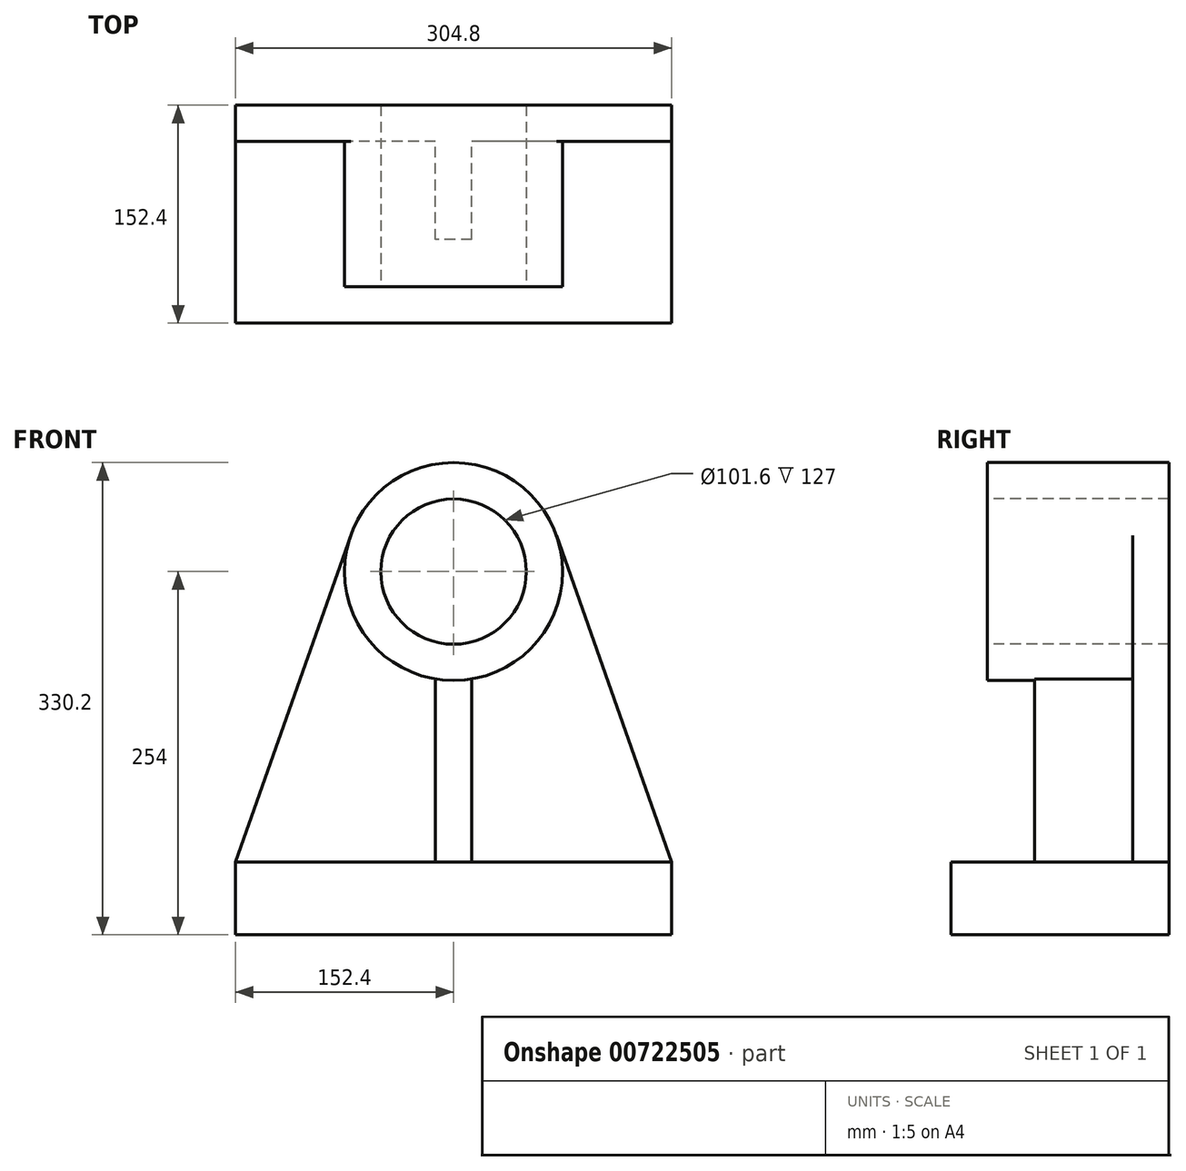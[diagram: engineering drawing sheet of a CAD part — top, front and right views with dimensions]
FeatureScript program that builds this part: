
annotation { "Feature Type Name" : "Feature", "Feature Type Description" : "" }
export const myFeature = defineFeature(function(context is Context, id is Id, definition is map)
    precondition{}
    {
        {
            var Q0;
            Q0=qCreatedBy(makeId("Top.planeOp"),FACE);
            var sketch = newSketch(context, id + "F0", { "sketchPlane" : qUnion([Q0])});
            skLineSegment(sketch, "E0.bottom", {"start": v(152.4, -76.2) * mm, "end": v(-152.4, -76.2) * mm});
            skLineSegment(sketch, "E0.top", {"start": v(152.4, 76.2) * mm, "end": v(-152.4, 76.2) * mm});
            skLineSegment(sketch, "E0.left", {"start": v(152.4, -76.2) * mm, "end": v(152.4, 76.2) * mm});
            skLineSegment(sketch, "E0.right", {"start": v(-152.4, -76.2) * mm, "end": v(-152.4, 76.2) * mm});
            skPoint(sketch, "E0.middle", {"position": v(0, 0) * mm});
            skSolve(sketch);
        }
        {
            var Q0;
            Q0 = qSketchRegion(id + "F0", true);
            extrude(context, id + "F1", {"entities" : qUnion([Q0]), "depth" : 50.8 * mm, "offsetDistance" : 25.4 * mm});
        }
        {
            var Q0;
            Q0=makeQuery(id+"F1.opExtrude","SWEPT_FACE",FACE,{"disambiguationData":[OSD([sQuery(id+"F0.wireOp",EDGE,"E0.top")])]});
            var sketch = newSketch(context, id + "F2", { "sketchPlane" : qUnion([Q0])});
            skLineSegment(sketch, "E1", {"start": v(0, 0) * mm, "end": v(0, 254) * mm, "construction": true});
            skLineSegment(sketch, "E2", {"start": v(-152.4, 50.8) * mm, "end": v(152.4, 50.8) * mm});
            skArc(sketch, "E3", {"start": v(71.87, 279.33) * mm, "mid": v(0, 330.2) * mm, "end": v(-71.87, 279.33) * mm});
            skLineSegment(sketch, "E4", {"start": v(-152.4, 50.8) * mm, "end": v(-71.87, 279.33) * mm});
            skLineSegment(sketch, "E5", {"start": v(152.4, 50.8) * mm, "end": v(71.87, 279.33) * mm});
            skSolve(sketch);
        }
        {
            var Q0;
            Q0 = qSketchRegion(id + "F2", true);
            extrude(context, id + "F3", {"entities" : qUnion([Q0]), "operationType" : NewBodyOperationType.ADD, "oppositeDirection" : true, "depth" : 25.4 * mm, "offsetDistance" : 25.4 * mm});
        }
        {
            var Q0;
            Q0=makeQuery(id+"F3.opExtrude","CAP_FACE",FACE,{"disambiguationData":[OSD([sQuery(id+"F2.wireOp",EDGE,"E2"),sQuery(id+"F2.wireOp",EDGE,"E3"),sQuery(id+"F2.wireOp",EDGE,"E4"),sQuery(id+"F2.wireOp",EDGE,"E5")])],"isStart":false});
            var sketch = newSketch(context, id + "F4", { "sketchPlane" : qUnion([Q0])});
            skCircle(sketch, "E6", {"center": v(0, 254) * mm, "radius": 76.2 * mm});
            skSolve(sketch);
        }
        {
            var Q0;
            Q0 = qSketchRegion(id + "F4", true);
            extrude(context, id + "F5", {"entities" : qUnion([Q0]), "operationType" : NewBodyOperationType.ADD, "depth" : 101.6 * mm, "offsetDistance" : 25.4 * mm});
        }
        {
            var Q0;
            Q0=makeQuery(id+"F5.opExtrude","CAP_FACE",FACE,{"disambiguationData":[OSD([sQuery(id+"F4.wireOp",EDGE,"E6")])],"isStart":false});
            var sketch = newSketch(context, id + "F6", { "sketchPlane" : qUnion([Q0])});
            skCircle(sketch, "E7.0", {"center": v(0, 254) * mm, "radius": 76.2 * mm, "construction": true});
            skCircle(sketch, "E8.0", {"center": v(0, 254) * mm, "radius": 50.8 * mm});
            skSolve(sketch);
        }
        {
            var Q0;
            Q0 = qSketchRegion(id + "F6", true);
            extrude(context, id + "F7", {"entities" : qUnion([Q0]), "operationType" : NewBodyOperationType.REMOVE, "endBound" : BoundingType.THROUGH_ALL, "oppositeDirection" : true, "depth" : 25.4 * mm, "offsetDistance" : 25.4 * mm});
        }
        {
            var Q0;
            Q0=makeQuery(id+"F3.opExtrude","CAP_FACE",FACE,{"disambiguationData":[OSD([sQuery(id+"F2.wireOp",EDGE,"E2"),sQuery(id+"F2.wireOp",EDGE,"E3"),sQuery(id+"F2.wireOp",EDGE,"E4"),sQuery(id+"F2.wireOp",EDGE,"E5")])],"isStart":false});
            var sketch = newSketch(context, id + "F8", { "sketchPlane" : qUnion([Q0])});
            skLineSegment(sketch, "E9", {"start": v(0, 0) * mm, "end": v(0, 254) * mm, "construction": true});
            skLineSegment(sketch, "E10", {"start": v(-12.7, 50.8) * mm, "end": v(-12.7, 178.87) * mm});
            skArc(sketch, "E11.0", {"start": v(-12.7, 178.87) * mm, "mid": v(0, 177.8) * mm, "end": v(12.7, 178.87) * mm});
            skLineSegment(sketch, "E12.MirrorCS", {"start": v(12.7, 50.8) * mm, "end": v(12.7, 178.87) * mm});
            skLineSegment(sketch, "E13", {"start": v(-12.7, 50.8) * mm, "end": v(12.7, 50.8) * mm});
            skPoint(sketch, "E14.orphan", {"position": v(-71.87, 279.33) * mm});
            skPoint(sketch, "E15.orphan", {"position": v(71.87, 279.33) * mm});
            skSolve(sketch);
        }
        {
            var Q0;
            Q0 = qSketchRegion(id + "F8", true);
            extrude(context, id + "F9", {"entities" : qUnion([Q0]), "operationType" : NewBodyOperationType.ADD, "depth" : 68.58 * mm, "offsetDistance" : 25.4 * mm});
        }
    });
